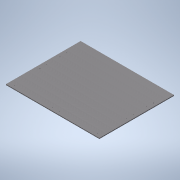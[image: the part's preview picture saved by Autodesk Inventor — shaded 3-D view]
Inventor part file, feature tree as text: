
AUTODESK INVENTOR PART (.ipt)
format: ipt  version: 2022 (Build 260153000, 153)  size: 130,048 bytes
history: native  units: mm
features: sketch x2, extrude x1, hole x1
ambient origin geometry x8: Origin, YZ Plane, XZ Plane, XY Plane, X Axis, Y Axis, Z Axis, Center Point
bodies: Solid1 (feature_tree)
feature tree (4):
  sketch  "Sketch1"  dims[d0=560.0mm d1=447.5mm]
  extrude  "Extrusion1"  Depth=447.5mm
  hole  "Hole1"  [1 undecoded]
  sketch  "Sketch2"  dims[d2=0.0mm d3=0.0mm d4=5.0mm d5=0.0mm d7=40.0mm d8=20.0mm d9=500.0mm d10=40.0mm d11=40.0mm d12=80.0mm d14=20.0mm d15=3.4mm d16=6.0mm d17=6.5mm d18=3.4mm d19=90.0deg d20=8.0mm d21=20.594885mm d23=40.0mm]
note: 1 required parameter value undecoded (feature->parameter linkage not recoverable at this tier; creation-order binding heuristic only, values carry confidence <= 0.55)
